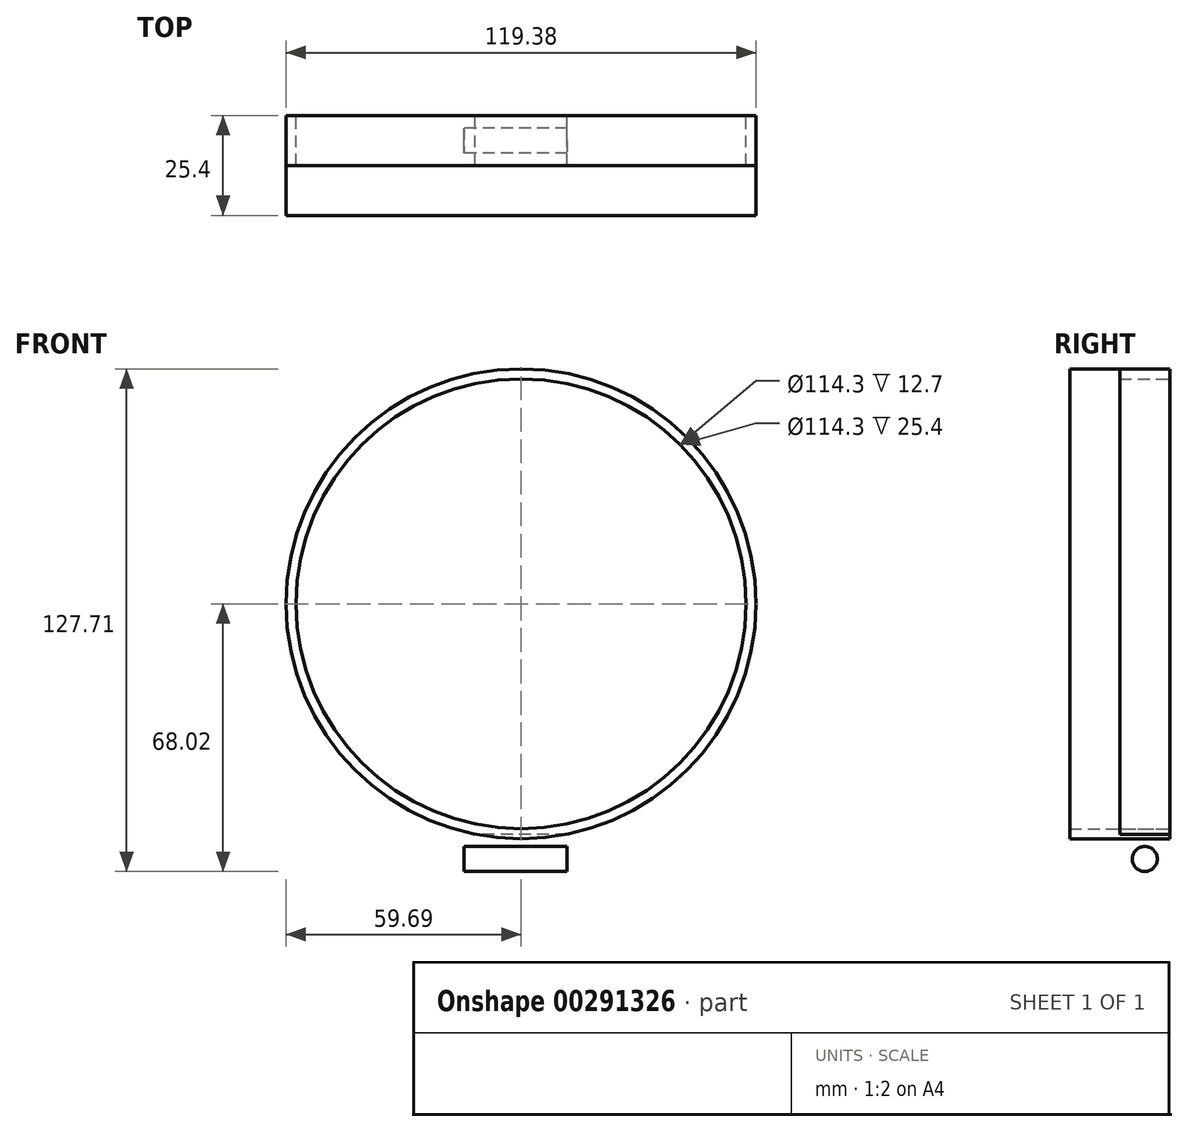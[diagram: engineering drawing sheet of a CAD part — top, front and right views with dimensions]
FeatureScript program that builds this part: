
annotation { "Feature Type Name" : "Feature", "Feature Type Description" : "" }
export const myFeature = defineFeature(function(context is Context, id is Id, definition is map)
    precondition{}
    {
        {
            var Q0;
            Q0=qCreatedBy(makeId("Front.planeOp"),FACE);
            var sketch = newSketch(context, id + "F0", { "sketchPlane" : qUnion([Q0])});
            skCircle(sketch, "E0", {"center": v(0, 0) * mm, "radius": 59.7 * mm});
            skCircle(sketch, "E1.0", {"center": v(0, 0) * mm, "radius": 57.15 * mm});
            skSolve(sketch);
        }
        {
            var Q0;
            Q0=makeQuery(id+"F0.imprint","IMPRINT",FACE,{"disambiguationData":[TD([[makeQuery(id+"F0.imprint","IMPRINT",EDGE,{"derivedFrom":sQuery(id+"F0.wireOp",EDGE,"E0")}),1.0]])]});
            extrude(context, id + "F1", {"entities" : qUnion([Q0]), "depth" : 12.7 * mm});
        }
        {
            var Q0;
            Q0=makeQuery(id+"F1.opExtrude","CAP_FACE",FACE,{"disambiguationData":[OSD([sQuery(id+"F0.wireOp",EDGE,"E0"),sQuery(id+"F0.wireOp",EDGE,"E1.0")])],"isStart":true});
            var sketch = newSketch(context, id + "F2", { "sketchPlane" : qUnion([Q0])});
            skLineSegment(sketch, "E2.bottom", {"start": v(-11.7, -58.53) * mm, "end": v(14.5, -58.53) * mm});
            skLineSegment(sketch, "E2.top", {"start": v(-11.7, -71.15) * mm, "end": v(14.5, -71.15) * mm});
            skLineSegment(sketch, "E2.left", {"start": v(-11.7, -58.53) * mm, "end": v(-11.7, -71.15) * mm});
            skLineSegment(sketch, "E2.right", {"start": v(14.5, -58.53) * mm, "end": v(14.5, -71.15) * mm});
            skSolve(sketch);
        }
        {
            var Q0;
            Q0=makeQuery(id+"F2.imprint","IMPRINT",FACE,{"disambiguationData":[TD([[makeQuery(id+"F2.imprint","IMPRINT",EDGE,{"derivedFrom":sQuery(id+"F2.wireOp",EDGE,"E2.top")}),1.0]])]});
            extrude(context, id + "F3", {"entities" : qUnion([Q0]), "oppositeDirection" : true, "depth" : 12.7 * mm});
        }
        {
            var Q0;
            Q0=makeQuery(id+"F3.opExtrude","SWEPT_FACE",FACE,{"disambiguationData":[OSD([sQuery(id+"F2.wireOp",EDGE,"E2.right")])]});
            var sketch = newSketch(context, id + "F4", { "sketchPlane" : qUnion([Q0])});
            skLineSegment(sketch, "E3", {"start": v(12.7, -71.15) * mm, "end": v(0, -58.53) * mm});
            skCircle(sketch, "E4", {"center": v(6.35, -64.84) * mm, "radius": 3.18 * mm});
            skSolve(sketch);
        }
        {
            var Q0;
            {var subQ0=sQuery(id+"F4.wireOp",EDGE,"E4");var subQ1=sQuery(id+"F4.wireOp",EDGE,"E3");var subQ2=makeQuery(id+"F4.imprint","INTERSECT",VERTEX,{"disambiguationData":[OD(0.0)],"derivedFrom":[subQ1,subQ0]});Q0=makeQuery(id+"F4.imprint","IMPRINT",FACE,{"disambiguationData":[TD([[makeQuery(id+"F4.imprint","IMPRINT",EDGE,{"disambiguationData":[TD([[subQ2,-1.0]])],"derivedFrom":subQ1}),1.0]])]});}
            var Q1;
            {var subQ0=sQuery(id+"F4.wireOp",EDGE,"E4");var subQ1=sQuery(id+"F4.wireOp",EDGE,"E3");var subQ2=makeQuery(id+"F4.imprint","INTERSECT",VERTEX,{"disambiguationData":[OD(0.0)],"derivedFrom":[subQ1,subQ0]});Q1=makeQuery(id+"F4.imprint","IMPRINT",FACE,{"disambiguationData":[TD([[makeQuery(id+"F4.imprint","IMPRINT",EDGE,{"disambiguationData":[TD([[subQ2,-1.0]])],"derivedFrom":subQ1}),-1.0]])]});}
            extrude(context, id + "F5", {"entities" : qUnion([Q0, Q1]), "operationType" : NewBodyOperationType.REMOVE, "oppositeDirection" : true, "depth" : 50.8 * mm});
        }
        {
            var Q0;
            Q0=makeQuery(id+"F0.imprint","IMPRINT",FACE,{"disambiguationData":[TD([[makeQuery(id+"F0.imprint","IMPRINT",EDGE,{"derivedFrom":sQuery(id+"F0.wireOp",EDGE,"E0")}),1.0]])]});
            extrude(context, id + "F6", {"entities" : qUnion([Q0]), "depth" : 25.4 * mm});
        }
    });
